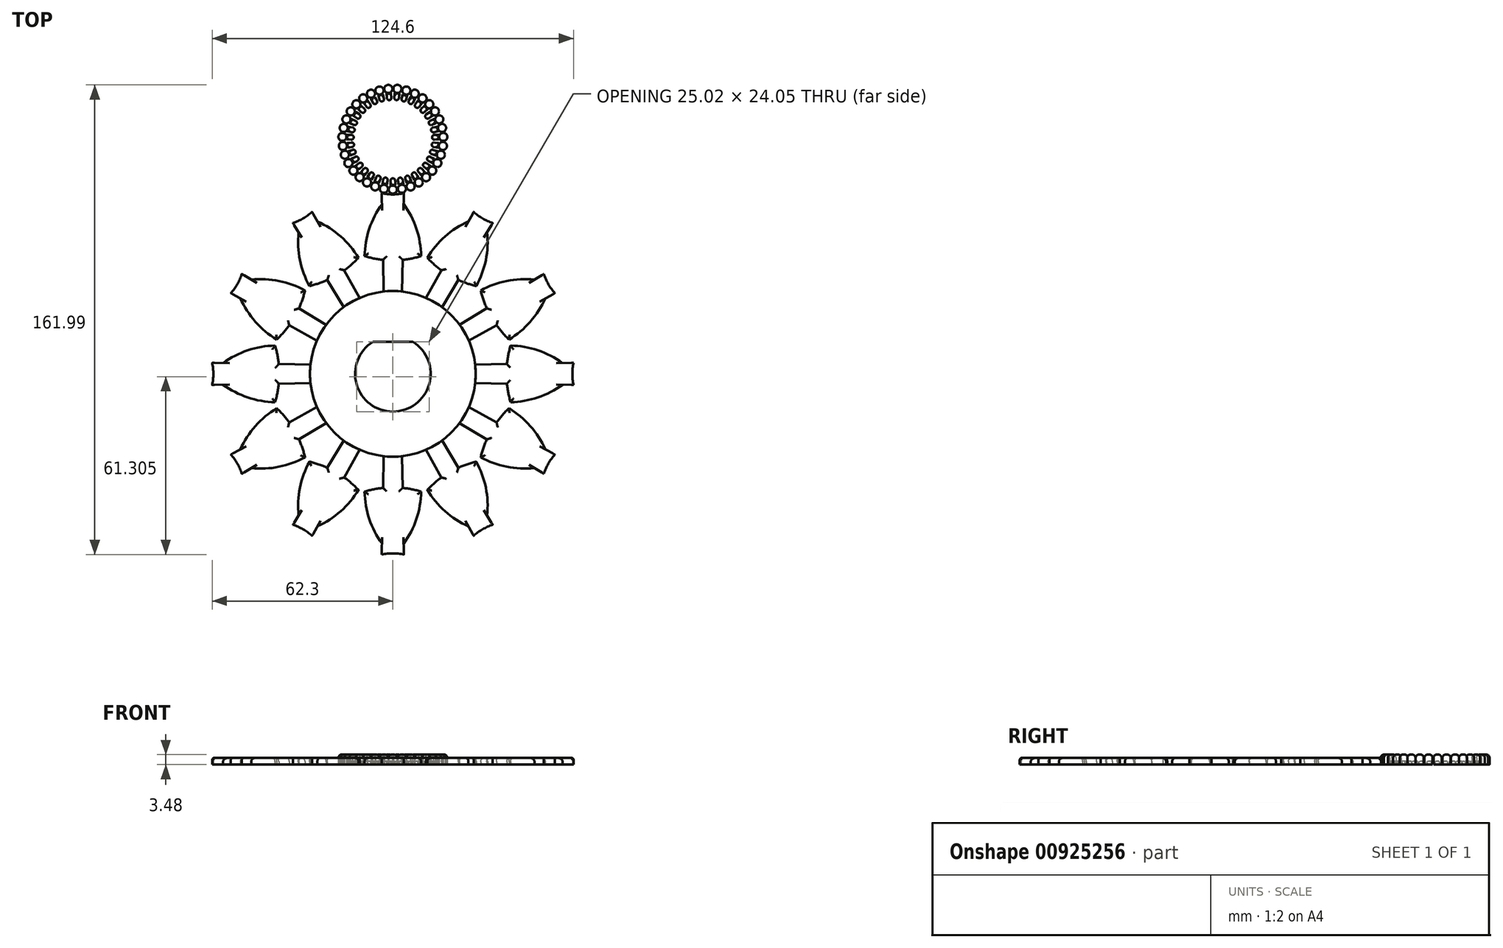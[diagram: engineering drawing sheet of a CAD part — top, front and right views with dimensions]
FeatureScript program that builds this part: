
annotation { "Feature Type Name" : "Feature", "Feature Type Description" : "" }
export const myFeature = defineFeature(function(context is Context, id is Id, definition is map)
    precondition{}
    {
        {
            var Q0;
            Q0=qCreatedBy(makeId("Top.planeOp"),FACE);
            var sketch = newSketch(context, id + "F0", { "sketchPlane" : qUnion([Q0])});
            skCircle(sketch, "E0", {"center": v(0, 0) * mm, "radius": 100.01 * mm, "construction": true});
            skCircle(sketch, "E1", {"center": v(0, 0) * mm, "radius": 80.96 * mm, "construction": true});
            skCircle(sketch, "E2", {"center": v(0, 0) * mm, "radius": 65.09 * mm, "construction": true});
            skCircle(sketch, "E3", {"center": v(0, 80.96) * mm, "radius": 19.05 * mm});
            skCircle(sketch, "E4.0", {"center": v(0, 80.96) * mm, "radius": 15.86 * mm});
            skArc(sketch, "E5", {"start": v(0.8, 66.65) * mm, "mid": v(0, 67.44) * mm, "end": v(-0.8, 66.65) * mm});
            skLineSegment(sketch, "E6", {"start": v(-0.8, 66.65) * mm, "end": v(-0.8, 65.12) * mm});
            skLineSegment(sketch, "E7", {"start": v(0.8, 66.65) * mm, "end": v(0.8, 65.12) * mm});
            skLineSegment(sketch, "E8.1.0", {"start": v(1.78, 66.73) * mm, "end": v(2.05, 65.24) * mm});
            skArc(sketch, "E8.1.1", {"start": v(3.34, 67.02) * mm, "mid": v(2.41, 67.66) * mm, "end": v(1.78, 66.73) * mm});
            skLineSegment(sketch, "E8.1.2", {"start": v(3.34, 67.02) * mm, "end": v(3.6, 65.52) * mm});
            skLineSegment(sketch, "E8.2.0", {"start": v(4.29, 67.28) * mm, "end": v(4.82, 65.85) * mm});
            skArc(sketch, "E8.2.1", {"start": v(5.77, 67.84) * mm, "mid": v(4.75, 68.3) * mm, "end": v(4.29, 67.28) * mm});
            skLineSegment(sketch, "E8.2.2", {"start": v(5.77, 67.84) * mm, "end": v(6.3, 66.41) * mm});
            skLineSegment(sketch, "E8.3.0", {"start": v(6.66, 68.27) * mm, "end": v(7.44, 66.96) * mm});
            skArc(sketch, "E8.3.1", {"start": v(8.02, 69.08) * mm, "mid": v(6.94, 69.35) * mm, "end": v(6.66, 68.27) * mm});
            skLineSegment(sketch, "E8.3.2", {"start": v(8.02, 69.08) * mm, "end": v(8.8, 67.77) * mm});
            skLineSegment(sketch, "E8.4.0", {"start": v(8.82, 69.66) * mm, "end": v(9.82, 68.51) * mm});
            skArc(sketch, "E8.4.1", {"start": v(10.02, 70.7) * mm, "mid": v(8.9, 70.78) * mm, "end": v(8.82, 69.66) * mm});
            skLineSegment(sketch, "E8.4.2", {"start": v(10.02, 70.7) * mm, "end": v(11.02, 69.56) * mm});
            skLineSegment(sketch, "E8.5.0", {"start": v(10.7, 71.42) * mm, "end": v(11.89, 70.47) * mm});
            skArc(sketch, "E8.5.1", {"start": v(11.69, 72.66) * mm, "mid": v(10.57, 72.53) * mm, "end": v(10.7, 71.42) * mm});
            skLineSegment(sketch, "E8.5.2", {"start": v(11.69, 72.66) * mm, "end": v(12.88, 71.7) * mm});
            skLineSegment(sketch, "E8.6.0", {"start": v(12.23, 73.48) * mm, "end": v(13.57, 72.76) * mm});
            skArc(sketch, "E8.6.1", {"start": v(12.98, 74.88) * mm, "mid": v(11.9, 74.55) * mm, "end": v(12.23, 73.48) * mm});
            skLineSegment(sketch, "E8.6.2", {"start": v(12.98, 74.88) * mm, "end": v(14.32, 74.16) * mm});
            skLineSegment(sketch, "E8.7.0", {"start": v(13.37, 75.78) * mm, "end": v(14.82, 75.31) * mm});
            skArc(sketch, "E8.7.1", {"start": v(13.86, 77.3) * mm, "mid": v(12.86, 76.78) * mm, "end": v(13.37, 75.78) * mm});
            skLineSegment(sketch, "E8.7.2", {"start": v(13.86, 77.3) * mm, "end": v(15.3, 76.82) * mm});
            skLineSegment(sketch, "E8.8.0", {"start": v(14.08, 78.25) * mm, "end": v(15.59, 78.05) * mm});
            skArc(sketch, "E8.8.1", {"start": v(14.3, 79.83) * mm, "mid": v(13.4, 79.15) * mm, "end": v(14.08, 78.25) * mm});
            skLineSegment(sketch, "E8.8.2", {"start": v(14.3, 79.83) * mm, "end": v(15.8, 79.62) * mm});
            skLineSegment(sketch, "E8.9.0", {"start": v(14.34, 80.81) * mm, "end": v(15.86, 80.88) * mm});
            skArc(sketch, "E8.9.1", {"start": v(14.27, 82.4) * mm, "mid": v(13.5, 81.57) * mm, "end": v(14.34, 80.81) * mm});
            skLineSegment(sketch, "E8.9.2", {"start": v(14.27, 82.4) * mm, "end": v(15.79, 82.47) * mm});
            skLineSegment(sketch, "E8.10.0", {"start": v(14.13, 83.37) * mm, "end": v(15.62, 83.71) * mm});
            skArc(sketch, "E8.10.1", {"start": v(13.78, 84.92) * mm, "mid": v(13.18, 83.97) * mm, "end": v(14.13, 83.37) * mm});
            skLineSegment(sketch, "E8.10.2", {"start": v(13.78, 84.92) * mm, "end": v(15.27, 85.26) * mm});
            skLineSegment(sketch, "E8.11.0", {"start": v(13.48, 85.86) * mm, "end": v(14.88, 86.46) * mm});
            skArc(sketch, "E8.11.1", {"start": v(12.85, 87.32) * mm, "mid": v(12.43, 86.28) * mm, "end": v(13.48, 85.86) * mm});
            skLineSegment(sketch, "E8.11.2", {"start": v(12.85, 87.32) * mm, "end": v(14.25, 87.92) * mm});
            skLineSegment(sketch, "E8.12.0", {"start": v(12.38, 88.19) * mm, "end": v(13.66, 89.03) * mm});
            skArc(sketch, "E8.12.1", {"start": v(11.51, 89.51) * mm, "mid": v(11.29, 88.41) * mm, "end": v(12.38, 88.19) * mm});
            skLineSegment(sketch, "E8.12.2", {"start": v(11.51, 89.51) * mm, "end": v(12.78, 90.35) * mm});
            skLineSegment(sketch, "E8.13.0", {"start": v(10.9, 90.28) * mm, "end": v(12, 91.34) * mm});
            skArc(sketch, "E8.13.1", {"start": v(9.8, 91.43) * mm, "mid": v(9.77, 90.3) * mm, "end": v(10.9, 90.28) * mm});
            skLineSegment(sketch, "E8.13.2", {"start": v(9.8, 91.43) * mm, "end": v(10.9, 92.48) * mm});
            skLineSegment(sketch, "E8.14.0", {"start": v(9.06, 92.08) * mm, "end": v(9.95, 93.31) * mm});
            skArc(sketch, "E8.14.1", {"start": v(7.77, 93.01) * mm, "mid": v(7.95, 91.9) * mm, "end": v(9.06, 92.08) * mm});
            skLineSegment(sketch, "E8.14.2", {"start": v(7.77, 93.01) * mm, "end": v(8.67, 94.24) * mm});
            skLineSegment(sketch, "E8.15.0", {"start": v(6.93, 93.52) * mm, "end": v(7.59, 94.89) * mm});
            skArc(sketch, "E8.15.1", {"start": v(5.5, 94.2) * mm, "mid": v(5.87, 93.15) * mm, "end": v(6.93, 93.52) * mm});
            skLineSegment(sketch, "E8.15.2", {"start": v(5.5, 94.2) * mm, "end": v(6.16, 95.58) * mm});
            skLineSegment(sketch, "E8.16.0", {"start": v(4.57, 94.55) * mm, "end": v(4.98, 96.02) * mm});
            skArc(sketch, "E8.16.1", {"start": v(3.04, 94.97) * mm, "mid": v(3.6, 94) * mm, "end": v(4.57, 94.55) * mm});
            skLineSegment(sketch, "E8.16.2", {"start": v(3.04, 94.97) * mm, "end": v(3.45, 96.44) * mm});
            skLineSegment(sketch, "E8.17.0", {"start": v(2.07, 95.15) * mm, "end": v(2.21, 96.67) * mm});
            skArc(sketch, "E8.17.1", {"start": v(0.5, 95.3) * mm, "mid": v(1.21, 94.43) * mm, "end": v(2.07, 95.15) * mm});
            skLineSegment(sketch, "E8.17.2", {"start": v(0.5, 95.3) * mm, "end": v(0.63, 96.8) * mm});
            skLineSegment(sketch, "E8.18.0", {"start": v(-0.5, 95.3) * mm, "end": v(-0.63, 96.8) * mm});
            skArc(sketch, "E8.18.1", {"start": v(-2.07, 95.15) * mm, "mid": v(-1.21, 94.43) * mm, "end": v(-0.5, 95.3) * mm});
            skLineSegment(sketch, "E8.18.2", {"start": v(-2.07, 95.15) * mm, "end": v(-2.21, 96.67) * mm});
            skLineSegment(sketch, "E8.19.0", {"start": v(-3.04, 94.97) * mm, "end": v(-3.45, 96.44) * mm});
            skArc(sketch, "E8.19.1", {"start": v(-4.57, 94.55) * mm, "mid": v(-3.6, 94) * mm, "end": v(-3.04, 94.97) * mm});
            skLineSegment(sketch, "E8.19.2", {"start": v(-4.57, 94.55) * mm, "end": v(-4.98, 96.02) * mm});
            skLineSegment(sketch, "E8.20.0", {"start": v(-5.5, 94.2) * mm, "end": v(-6.16, 95.58) * mm});
            skArc(sketch, "E8.20.1", {"start": v(-6.93, 93.52) * mm, "mid": v(-5.87, 93.15) * mm, "end": v(-5.5, 94.2) * mm});
            skLineSegment(sketch, "E8.20.2", {"start": v(-6.93, 93.52) * mm, "end": v(-7.59, 94.89) * mm});
            skLineSegment(sketch, "E8.21.0", {"start": v(-7.77, 93.01) * mm, "end": v(-8.67, 94.24) * mm});
            skArc(sketch, "E8.21.1", {"start": v(-9.06, 92.08) * mm, "mid": v(-7.95, 91.9) * mm, "end": v(-7.77, 93.01) * mm});
            skLineSegment(sketch, "E8.21.2", {"start": v(-9.06, 92.08) * mm, "end": v(-9.95, 93.31) * mm});
            skLineSegment(sketch, "E8.22.0", {"start": v(-9.8, 91.43) * mm, "end": v(-10.9, 92.48) * mm});
            skArc(sketch, "E8.22.1", {"start": v(-10.9, 90.28) * mm, "mid": v(-9.77, 90.3) * mm, "end": v(-9.8, 91.43) * mm});
            skLineSegment(sketch, "E8.22.2", {"start": v(-10.9, 90.28) * mm, "end": v(-12, 91.34) * mm});
            skLineSegment(sketch, "E8.23.0", {"start": v(-11.51, 89.51) * mm, "end": v(-12.78, 90.35) * mm});
            skArc(sketch, "E8.23.1", {"start": v(-12.38, 88.19) * mm, "mid": v(-11.29, 88.41) * mm, "end": v(-11.51, 89.51) * mm});
            skLineSegment(sketch, "E8.23.2", {"start": v(-12.38, 88.19) * mm, "end": v(-13.66, 89.03) * mm});
            skLineSegment(sketch, "E8.24.0", {"start": v(-12.85, 87.32) * mm, "end": v(-14.25, 87.92) * mm});
            skArc(sketch, "E8.24.1", {"start": v(-13.48, 85.86) * mm, "mid": v(-12.43, 86.28) * mm, "end": v(-12.85, 87.32) * mm});
            skLineSegment(sketch, "E8.24.2", {"start": v(-13.48, 85.86) * mm, "end": v(-14.88, 86.46) * mm});
            skLineSegment(sketch, "E8.25.0", {"start": v(-13.78, 84.92) * mm, "end": v(-15.27, 85.26) * mm});
            skArc(sketch, "E8.25.1", {"start": v(-14.13, 83.37) * mm, "mid": v(-13.18, 83.97) * mm, "end": v(-13.78, 84.92) * mm});
            skLineSegment(sketch, "E8.25.2", {"start": v(-14.13, 83.37) * mm, "end": v(-15.62, 83.71) * mm});
            skLineSegment(sketch, "E8.26.0", {"start": v(-14.27, 82.4) * mm, "end": v(-15.79, 82.47) * mm});
            skArc(sketch, "E8.26.1", {"start": v(-14.34, 80.81) * mm, "mid": v(-13.5, 81.57) * mm, "end": v(-14.27, 82.4) * mm});
            skLineSegment(sketch, "E8.26.2", {"start": v(-14.34, 80.81) * mm, "end": v(-15.86, 80.88) * mm});
            skLineSegment(sketch, "E8.27.0", {"start": v(-14.3, 79.83) * mm, "end": v(-15.8, 79.62) * mm});
            skArc(sketch, "E8.27.1", {"start": v(-14.08, 78.25) * mm, "mid": v(-13.4, 79.15) * mm, "end": v(-14.3, 79.83) * mm});
            skLineSegment(sketch, "E8.27.2", {"start": v(-14.08, 78.25) * mm, "end": v(-15.59, 78.05) * mm});
            skLineSegment(sketch, "E8.28.0", {"start": v(-13.86, 77.3) * mm, "end": v(-15.3, 76.82) * mm});
            skArc(sketch, "E8.28.1", {"start": v(-13.37, 75.78) * mm, "mid": v(-12.86, 76.78) * mm, "end": v(-13.86, 77.3) * mm});
            skLineSegment(sketch, "E8.28.2", {"start": v(-13.37, 75.78) * mm, "end": v(-14.82, 75.31) * mm});
            skLineSegment(sketch, "E8.29.0", {"start": v(-12.98, 74.88) * mm, "end": v(-14.32, 74.16) * mm});
            skArc(sketch, "E8.29.1", {"start": v(-12.23, 73.48) * mm, "mid": v(-11.9, 74.55) * mm, "end": v(-12.98, 74.88) * mm});
            skLineSegment(sketch, "E8.29.2", {"start": v(-12.23, 73.48) * mm, "end": v(-13.57, 72.76) * mm});
            skLineSegment(sketch, "E8.30.0", {"start": v(-11.69, 72.66) * mm, "end": v(-12.88, 71.7) * mm});
            skArc(sketch, "E8.30.1", {"start": v(-10.7, 71.42) * mm, "mid": v(-10.57, 72.53) * mm, "end": v(-11.69, 72.66) * mm});
            skLineSegment(sketch, "E8.30.2", {"start": v(-10.7, 71.42) * mm, "end": v(-11.89, 70.47) * mm});
            skLineSegment(sketch, "E8.31.0", {"start": v(-10.02, 70.7) * mm, "end": v(-11.02, 69.56) * mm});
            skArc(sketch, "E8.31.1", {"start": v(-8.82, 69.66) * mm, "mid": v(-8.9, 70.78) * mm, "end": v(-10.02, 70.7) * mm});
            skLineSegment(sketch, "E8.31.2", {"start": v(-8.82, 69.66) * mm, "end": v(-9.82, 68.51) * mm});
            skLineSegment(sketch, "E8.32.0", {"start": v(-8.02, 69.08) * mm, "end": v(-8.8, 67.77) * mm});
            skArc(sketch, "E8.32.1", {"start": v(-6.66, 68.27) * mm, "mid": v(-6.94, 69.35) * mm, "end": v(-8.02, 69.08) * mm});
            skLineSegment(sketch, "E8.32.2", {"start": v(-6.66, 68.27) * mm, "end": v(-7.44, 66.96) * mm});
            skLineSegment(sketch, "E8.33.0", {"start": v(-5.77, 67.84) * mm, "end": v(-6.3, 66.41) * mm});
            skArc(sketch, "E8.33.1", {"start": v(-4.29, 67.28) * mm, "mid": v(-4.75, 68.3) * mm, "end": v(-5.77, 67.84) * mm});
            skLineSegment(sketch, "E8.33.2", {"start": v(-4.29, 67.28) * mm, "end": v(-4.82, 65.85) * mm});
            skLineSegment(sketch, "E8.34.0", {"start": v(-3.34, 67.02) * mm, "end": v(-3.6, 65.52) * mm});
            skArc(sketch, "E8.34.1", {"start": v(-1.78, 66.73) * mm, "mid": v(-2.41, 67.66) * mm, "end": v(-3.34, 67.02) * mm});
            skLineSegment(sketch, "E8.34.2", {"start": v(-1.78, 66.73) * mm, "end": v(-2.05, 65.24) * mm});
            skCircle(sketch, "E9", {"center": v(0, 63.56) * mm, "radius": 1.4 * mm});
            skCircle(sketch, "E10.1.0", {"center": v(3.1, 63.84) * mm, "radius": 1.4 * mm});
            skCircle(sketch, "E10.2.0", {"center": v(6.11, 64.67) * mm, "radius": 1.4 * mm});
            skCircle(sketch, "E10.3.0", {"center": v(8.92, 66.03) * mm, "radius": 1.4 * mm});
            skCircle(sketch, "E10.4.0", {"center": v(11.45, 67.86) * mm, "radius": 1.4 * mm});
            skCircle(sketch, "E10.5.0", {"center": v(13.6, 70.11) * mm, "radius": 1.4 * mm});
            skCircle(sketch, "E10.6.0", {"center": v(15.32, 72.72) * mm, "radius": 1.4 * mm});
            skCircle(sketch, "E10.7.0", {"center": v(16.55, 75.59) * mm, "radius": 1.4 * mm});
            skCircle(sketch, "E10.8.0", {"center": v(17.24, 78.63) * mm, "radius": 1.4 * mm});
            skCircle(sketch, "E10.9.0", {"center": v(17.38, 81.74) * mm, "radius": 1.4 * mm});
            skCircle(sketch, "E10.10.0", {"center": v(16.96, 84.83) * mm, "radius": 1.4 * mm});
            skCircle(sketch, "E10.11.0", {"center": v(16, 87.8) * mm, "radius": 1.4 * mm});
            skCircle(sketch, "E10.12.0", {"center": v(14.52, 90.55) * mm, "radius": 1.4 * mm});
            skCircle(sketch, "E10.13.0", {"center": v(12.58, 92.99) * mm, "radius": 1.4 * mm});
            skCircle(sketch, "E10.14.0", {"center": v(10.23, 95.04) * mm, "radius": 1.4 * mm});
            skCircle(sketch, "E10.15.0", {"center": v(7.55, 96.64) * mm, "radius": 1.4 * mm});
            skCircle(sketch, "E10.16.0", {"center": v(4.63, 97.73) * mm, "radius": 1.4 * mm});
            skCircle(sketch, "E10.17.0", {"center": v(1.56, 98.3) * mm, "radius": 1.4 * mm});
            skCircle(sketch, "E10.18.0", {"center": v(-1.56, 98.3) * mm, "radius": 1.4 * mm});
            skCircle(sketch, "E10.19.0", {"center": v(-4.63, 97.73) * mm, "radius": 1.4 * mm});
            skCircle(sketch, "E10.20.0", {"center": v(-7.55, 96.64) * mm, "radius": 1.4 * mm});
            skCircle(sketch, "E10.21.0", {"center": v(-10.23, 95.04) * mm, "radius": 1.4 * mm});
            skCircle(sketch, "E10.22.0", {"center": v(-12.58, 92.99) * mm, "radius": 1.4 * mm});
            skCircle(sketch, "E10.23.0", {"center": v(-14.52, 90.55) * mm, "radius": 1.4 * mm});
            skCircle(sketch, "E10.24.0", {"center": v(-16, 87.8) * mm, "radius": 1.4 * mm});
            skCircle(sketch, "E10.25.0", {"center": v(-16.96, 84.83) * mm, "radius": 1.4 * mm});
            skCircle(sketch, "E10.26.0", {"center": v(-17.38, 81.74) * mm, "radius": 1.4 * mm});
            skCircle(sketch, "E10.27.0", {"center": v(-17.24, 78.63) * mm, "radius": 1.4 * mm});
            skCircle(sketch, "E10.28.0", {"center": v(-16.55, 75.59) * mm, "radius": 1.4 * mm});
            skCircle(sketch, "E10.29.0", {"center": v(-15.32, 72.72) * mm, "radius": 1.4 * mm});
            skCircle(sketch, "E10.30.0", {"center": v(-13.6, 70.11) * mm, "radius": 1.4 * mm});
            skCircle(sketch, "E10.31.0", {"center": v(-11.45, 67.86) * mm, "radius": 1.4 * mm});
            skCircle(sketch, "E10.32.0", {"center": v(-8.92, 66.03) * mm, "radius": 1.4 * mm});
            skCircle(sketch, "E10.33.0", {"center": v(-6.11, 64.67) * mm, "radius": 1.4 * mm});
            skCircle(sketch, "E10.34.0", {"center": v(-3.1, 63.84) * mm, "radius": 1.4 * mm});
            skLineSegment(sketch, "E11.0", {"start": v(3.18, 28.4) * mm, "end": v(3.81, 62.3) * mm});
            skLineSegment(sketch, "E12.0", {"start": v(-3.18, 28.4) * mm, "end": v(-3.81, 62.3) * mm});
            skCircle(sketch, "E13", {"center": v(0, 0) * mm, "radius": 28.58 * mm});
            skLineSegment(sketch, "E14.0", {"start": v(9.44, 23.59) * mm, "end": v(10.16, 62.18) * mm, "construction": true});
            skLineSegment(sketch, "E15.0", {"start": v(-9.44, 23.59) * mm, "end": v(-10.16, 62.18) * mm, "construction": true});
            skLineSegment(sketch, "E16", {"start": v(-12.43, 40.62) * mm, "end": v(16.46, 40.62) * mm, "construction": true});
            skLineSegment(sketch, "E17", {"start": v(-3.74, 58.53) * mm, "end": v(3.74, 58.53) * mm, "construction": true});
            skArc(sketch, "E18", {"start": v(-3.74, 58.53) * mm, "mid": v(-8.13, 50.03) * mm, "end": v(-9.75, 40.62) * mm});
            skArc(sketch, "E19", {"start": v(9.75, 40.62) * mm, "mid": v(8.12, 50.03) * mm, "end": v(3.74, 58.53) * mm});
            skArc(sketch, "E20", {"start": v(-9.75, 40.62) * mm, "mid": v(0, 39.17) * mm, "end": v(9.75, 40.62) * mm});
            skSolve(sketch);
        }
        {
            var Q0;
            {var subQ0=sQuery(id+"F0.wireOp",EDGE,"E13");var subQ1=sQuery(id+"F0.wireOp",EDGE,"E11.0");var subQ2=makeQuery(id+"F0.imprint","INTERSECT",VERTEX,{"derivedFrom":[subQ1,subQ0]});Q0=makeQuery(id+"F0.imprint","IMPRINT",FACE,{"disambiguationData":[TD([[makeQuery(id+"F0.imprint","IMPRINT",EDGE,{"disambiguationData":[TD([[subQ2,-1.0]])],"derivedFrom":subQ1}),1.0]])]});}
            var Q1;
            {var subQ4=sQuery(id+"F0.wireOp",EDGE,"E11.0");var subQ5=sQuery(id+"F0.wireOp",EDGE,"E3");var subQ6=makeQuery(id+"F0.imprint","INTERSECT",VERTEX,{"derivedFrom":[subQ5,subQ4]});Q1=makeQuery(id+"F0.imprint","IMPRINT",FACE,{"disambiguationData":[TD([[makeQuery(id+"F0.imprint","IMPRINT",EDGE,{"disambiguationData":[TD([[subQ6,1.0]])],"derivedFrom":subQ5}),-1.0]])]});}
            var Q2;
            {var subQ0=sQuery(id+"F0.wireOp",EDGE,"E19");Q2=makeQuery(id+"F0.imprint","IMPRINT",FACE,{"disambiguationData":[TD([[makeQuery(id+"F0.imprint","IMPRINT",EDGE,{"derivedFrom":subQ0}),1.0]])]});}
            var Q3;
            {var subQ0=sQuery(id+"F0.wireOp",EDGE,"E18");Q3=makeQuery(id+"F0.imprint","IMPRINT",FACE,{"disambiguationData":[TD([[makeQuery(id+"F0.imprint","IMPRINT",EDGE,{"derivedFrom":subQ0}),1.0]])]});}
            var Q4;
            Q4=makeQuery(id+"F0.imprint","IMPRINT",FACE,{"disambiguationData":[TD([[makeQuery(id+"F0.imprint","IMPRINT",EDGE,{"derivedFrom":sQuery(id+"F0.wireOp",EDGE,"E9")}),-1.0]])]});
            extrude(context, id + "F1", {"entities" : qUnion([Q0, Q1, Q2, Q3, Q4]), "depth" : 2.38 * mm, "offsetDistance" : 25.4 * mm});
        }
        {
            var Q0;
            Q0=makeQuery(id+"F0.imprint","IMPRINT",FACE,{"disambiguationData":[TD([[makeQuery(id+"F0.imprint","IMPRINT",EDGE,{"derivedFrom":sQuery(id+"F0.wireOp",EDGE,"E10.22.0")}),1.0]])]});
            var Q1;
            Q1=makeQuery(id+"F0.imprint","IMPRINT",FACE,{"disambiguationData":[TD([[makeQuery(id+"F0.imprint","IMPRINT",EDGE,{"derivedFrom":sQuery(id+"F0.wireOp",EDGE,"E10.21.0")}),1.0]])]});
            var Q2;
            Q2=makeQuery(id+"F0.imprint","IMPRINT",FACE,{"disambiguationData":[TD([[makeQuery(id+"F0.imprint","IMPRINT",EDGE,{"derivedFrom":sQuery(id+"F0.wireOp",EDGE,"E10.19.0")}),1.0]])]});
            var Q3;
            Q3=makeQuery(id+"F0.imprint","IMPRINT",FACE,{"disambiguationData":[TD([[makeQuery(id+"F0.imprint","IMPRINT",EDGE,{"derivedFrom":sQuery(id+"F0.wireOp",EDGE,"E10.18.0")}),1.0]])]});
            var Q4;
            Q4=makeQuery(id+"F0.imprint","IMPRINT",FACE,{"disambiguationData":[TD([[makeQuery(id+"F0.imprint","IMPRINT",EDGE,{"derivedFrom":sQuery(id+"F0.wireOp",EDGE,"E10.20.0")}),1.0]])]});
            var Q5;
            Q5=makeQuery(id+"F0.imprint","IMPRINT",FACE,{"disambiguationData":[TD([[makeQuery(id+"F0.imprint","IMPRINT",EDGE,{"derivedFrom":sQuery(id+"F0.wireOp",EDGE,"E10.17.0")}),1.0]])]});
            var Q6;
            Q6=makeQuery(id+"F0.imprint","IMPRINT",FACE,{"disambiguationData":[TD([[makeQuery(id+"F0.imprint","IMPRINT",EDGE,{"derivedFrom":sQuery(id+"F0.wireOp",EDGE,"E10.16.0")}),1.0]])]});
            var Q7;
            Q7=makeQuery(id+"F0.imprint","IMPRINT",FACE,{"disambiguationData":[TD([[makeQuery(id+"F0.imprint","IMPRINT",EDGE,{"derivedFrom":sQuery(id+"F0.wireOp",EDGE,"E10.15.0")}),1.0]])]});
            var Q8;
            Q8=makeQuery(id+"F0.imprint","IMPRINT",FACE,{"disambiguationData":[TD([[makeQuery(id+"F0.imprint","IMPRINT",EDGE,{"derivedFrom":sQuery(id+"F0.wireOp",EDGE,"E10.14.0")}),1.0]])]});
            var Q9;
            Q9=makeQuery(id+"F0.imprint","IMPRINT",FACE,{"disambiguationData":[TD([[makeQuery(id+"F0.imprint","IMPRINT",EDGE,{"derivedFrom":sQuery(id+"F0.wireOp",EDGE,"E10.13.0")}),1.0]])]});
            var Q10;
            Q10=makeQuery(id+"F0.imprint","IMPRINT",FACE,{"disambiguationData":[TD([[makeQuery(id+"F0.imprint","IMPRINT",EDGE,{"derivedFrom":sQuery(id+"F0.wireOp",EDGE,"E10.12.0")}),1.0]])]});
            var Q11;
            Q11=makeQuery(id+"F0.imprint","IMPRINT",FACE,{"disambiguationData":[TD([[makeQuery(id+"F0.imprint","IMPRINT",EDGE,{"derivedFrom":sQuery(id+"F0.wireOp",EDGE,"E10.11.0")}),1.0]])]});
            var Q12;
            Q12=makeQuery(id+"F0.imprint","IMPRINT",FACE,{"disambiguationData":[TD([[makeQuery(id+"F0.imprint","IMPRINT",EDGE,{"derivedFrom":sQuery(id+"F0.wireOp",EDGE,"E10.10.0")}),1.0]])]});
            var Q13;
            Q13=makeQuery(id+"F0.imprint","IMPRINT",FACE,{"disambiguationData":[TD([[makeQuery(id+"F0.imprint","IMPRINT",EDGE,{"derivedFrom":sQuery(id+"F0.wireOp",EDGE,"E10.9.0")}),1.0]])]});
            var Q14;
            Q14=makeQuery(id+"F0.imprint","IMPRINT",FACE,{"disambiguationData":[TD([[makeQuery(id+"F0.imprint","IMPRINT",EDGE,{"derivedFrom":sQuery(id+"F0.wireOp",EDGE,"E10.8.0")}),1.0]])]});
            var Q15;
            Q15=makeQuery(id+"F0.imprint","IMPRINT",FACE,{"disambiguationData":[TD([[makeQuery(id+"F0.imprint","IMPRINT",EDGE,{"derivedFrom":sQuery(id+"F0.wireOp",EDGE,"E10.23.0")}),1.0]])]});
            var Q16;
            Q16=makeQuery(id+"F0.imprint","IMPRINT",FACE,{"disambiguationData":[TD([[makeQuery(id+"F0.imprint","IMPRINT",EDGE,{"derivedFrom":sQuery(id+"F0.wireOp",EDGE,"E10.24.0")}),1.0]])]});
            var Q17;
            Q17=makeQuery(id+"F0.imprint","IMPRINT",FACE,{"disambiguationData":[TD([[makeQuery(id+"F0.imprint","IMPRINT",EDGE,{"derivedFrom":sQuery(id+"F0.wireOp",EDGE,"E10.25.0")}),1.0]])]});
            var Q18;
            Q18=makeQuery(id+"F0.imprint","IMPRINT",FACE,{"disambiguationData":[TD([[makeQuery(id+"F0.imprint","IMPRINT",EDGE,{"derivedFrom":sQuery(id+"F0.wireOp",EDGE,"E10.26.0")}),1.0]])]});
            var Q19;
            Q19=makeQuery(id+"F0.imprint","IMPRINT",FACE,{"disambiguationData":[TD([[makeQuery(id+"F0.imprint","IMPRINT",EDGE,{"derivedFrom":sQuery(id+"F0.wireOp",EDGE,"E10.27.0")}),1.0]])]});
            var Q20;
            Q20=makeQuery(id+"F0.imprint","IMPRINT",FACE,{"disambiguationData":[TD([[makeQuery(id+"F0.imprint","IMPRINT",EDGE,{"derivedFrom":sQuery(id+"F0.wireOp",EDGE,"E10.28.0")}),1.0]])]});
            var Q21;
            Q21=makeQuery(id+"F0.imprint","IMPRINT",FACE,{"disambiguationData":[TD([[makeQuery(id+"F0.imprint","IMPRINT",EDGE,{"derivedFrom":sQuery(id+"F0.wireOp",EDGE,"E10.29.0")}),1.0]])]});
            var Q22;
            Q22=makeQuery(id+"F0.imprint","IMPRINT",FACE,{"disambiguationData":[TD([[makeQuery(id+"F0.imprint","IMPRINT",EDGE,{"derivedFrom":sQuery(id+"F0.wireOp",EDGE,"E10.30.0")}),1.0]])]});
            var Q23;
            Q23=makeQuery(id+"F0.imprint","IMPRINT",FACE,{"disambiguationData":[TD([[makeQuery(id+"F0.imprint","IMPRINT",EDGE,{"derivedFrom":sQuery(id+"F0.wireOp",EDGE,"E10.31.0")}),1.0]])]});
            var Q24;
            Q24=makeQuery(id+"F0.imprint","IMPRINT",FACE,{"disambiguationData":[TD([[makeQuery(id+"F0.imprint","IMPRINT",EDGE,{"derivedFrom":sQuery(id+"F0.wireOp",EDGE,"E10.33.0")}),1.0]])]});
            var Q25;
            Q25=makeQuery(id+"F0.imprint","IMPRINT",FACE,{"disambiguationData":[TD([[makeQuery(id+"F0.imprint","IMPRINT",EDGE,{"derivedFrom":sQuery(id+"F0.wireOp",EDGE,"E10.34.0")}),1.0]])]});
            var Q26;
            Q26=makeQuery(id+"F0.imprint","IMPRINT",FACE,{"disambiguationData":[TD([[makeQuery(id+"F0.imprint","IMPRINT",EDGE,{"derivedFrom":sQuery(id+"F0.wireOp",EDGE,"E9")}),1.0]])]});
            var Q27;
            Q27=makeQuery(id+"F0.imprint","IMPRINT",FACE,{"disambiguationData":[TD([[makeQuery(id+"F0.imprint","IMPRINT",EDGE,{"derivedFrom":sQuery(id+"F0.wireOp",EDGE,"E10.32.0")}),1.0]])]});
            var Q28;
            Q28=makeQuery(id+"F0.imprint","IMPRINT",FACE,{"disambiguationData":[TD([[makeQuery(id+"F0.imprint","IMPRINT",EDGE,{"derivedFrom":sQuery(id+"F0.wireOp",EDGE,"E10.1.0")}),1.0]])]});
            var Q29;
            Q29=makeQuery(id+"F0.imprint","IMPRINT",FACE,{"disambiguationData":[TD([[makeQuery(id+"F0.imprint","IMPRINT",EDGE,{"derivedFrom":sQuery(id+"F0.wireOp",EDGE,"E10.2.0")}),1.0]])]});
            var Q30;
            Q30=makeQuery(id+"F0.imprint","IMPRINT",FACE,{"disambiguationData":[TD([[makeQuery(id+"F0.imprint","IMPRINT",EDGE,{"derivedFrom":sQuery(id+"F0.wireOp",EDGE,"E10.3.0")}),1.0]])]});
            var Q31;
            Q31=makeQuery(id+"F0.imprint","IMPRINT",FACE,{"disambiguationData":[TD([[makeQuery(id+"F0.imprint","IMPRINT",EDGE,{"derivedFrom":sQuery(id+"F0.wireOp",EDGE,"E10.4.0")}),1.0]])]});
            var Q32;
            Q32=makeQuery(id+"F0.imprint","IMPRINT",FACE,{"disambiguationData":[TD([[makeQuery(id+"F0.imprint","IMPRINT",EDGE,{"derivedFrom":sQuery(id+"F0.wireOp",EDGE,"E10.5.0")}),1.0]])]});
            var Q33;
            Q33=makeQuery(id+"F0.imprint","IMPRINT",FACE,{"disambiguationData":[TD([[makeQuery(id+"F0.imprint","IMPRINT",EDGE,{"derivedFrom":sQuery(id+"F0.wireOp",EDGE,"E10.6.0")}),1.0]])]});
            var Q34;
            Q34=makeQuery(id+"F0.imprint","IMPRINT",FACE,{"disambiguationData":[TD([[makeQuery(id+"F0.imprint","IMPRINT",EDGE,{"derivedFrom":sQuery(id+"F0.wireOp",EDGE,"E10.7.0")}),1.0]])]});
            extrude(context, id + "F2", {"entities" : qUnion([Q0, Q1, Q2, Q3, Q4, Q5, Q6, Q7, Q8, Q9, Q10, Q11, Q12, Q13, Q14, Q15, Q16, Q17, Q18, Q19, Q20, Q21, Q22, Q23, Q24, Q25, Q26, Q27, Q28, Q29, Q30, Q31, Q32, Q33, Q34]), "operationType" : NewBodyOperationType.ADD, "depth" : 3.48 * mm, "offsetDistance" : 25.4 * mm});
        }
        {
            var Q0;
            {var subQ0=sQuery(id+"F0.wireOp",EDGE,"E8.25.0");Q0=makeQuery(id+"F0.imprint","IMPRINT",FACE,{"disambiguationData":[TD([[makeQuery(id+"F0.imprint","IMPRINT",EDGE,{"derivedFrom":subQ0}),1.0]])]});}
            var Q1;
            {var subQ0=sQuery(id+"F0.wireOp",EDGE,"E8.24.0");Q1=makeQuery(id+"F0.imprint","IMPRINT",FACE,{"disambiguationData":[TD([[makeQuery(id+"F0.imprint","IMPRINT",EDGE,{"derivedFrom":subQ0}),1.0]])]});}
            var Q2;
            {var subQ0=sQuery(id+"F0.wireOp",EDGE,"E8.26.0");Q2=makeQuery(id+"F0.imprint","IMPRINT",FACE,{"disambiguationData":[TD([[makeQuery(id+"F0.imprint","IMPRINT",EDGE,{"derivedFrom":subQ0}),1.0]])]});}
            var Q3;
            {var subQ0=sQuery(id+"F0.wireOp",EDGE,"E8.27.0");Q3=makeQuery(id+"F0.imprint","IMPRINT",FACE,{"disambiguationData":[TD([[makeQuery(id+"F0.imprint","IMPRINT",EDGE,{"derivedFrom":subQ0}),1.0]])]});}
            var Q4;
            {var subQ0=sQuery(id+"F0.wireOp",EDGE,"E8.28.0");Q4=makeQuery(id+"F0.imprint","IMPRINT",FACE,{"disambiguationData":[TD([[makeQuery(id+"F0.imprint","IMPRINT",EDGE,{"derivedFrom":subQ0}),1.0]])]});}
            var Q5;
            {var subQ0=sQuery(id+"F0.wireOp",EDGE,"E8.29.0");Q5=makeQuery(id+"F0.imprint","IMPRINT",FACE,{"disambiguationData":[TD([[makeQuery(id+"F0.imprint","IMPRINT",EDGE,{"derivedFrom":subQ0}),1.0]])]});}
            var Q6;
            {var subQ0=sQuery(id+"F0.wireOp",EDGE,"E8.30.0");Q6=makeQuery(id+"F0.imprint","IMPRINT",FACE,{"disambiguationData":[TD([[makeQuery(id+"F0.imprint","IMPRINT",EDGE,{"derivedFrom":subQ0}),1.0]])]});}
            var Q7;
            {var subQ0=sQuery(id+"F0.wireOp",EDGE,"E8.31.0");Q7=makeQuery(id+"F0.imprint","IMPRINT",FACE,{"disambiguationData":[TD([[makeQuery(id+"F0.imprint","IMPRINT",EDGE,{"derivedFrom":subQ0}),1.0]])]});}
            var Q8;
            {var subQ0=sQuery(id+"F0.wireOp",EDGE,"E8.32.0");Q8=makeQuery(id+"F0.imprint","IMPRINT",FACE,{"disambiguationData":[TD([[makeQuery(id+"F0.imprint","IMPRINT",EDGE,{"derivedFrom":subQ0}),1.0]])]});}
            var Q9;
            {var subQ0=sQuery(id+"F0.wireOp",EDGE,"E8.33.0");Q9=makeQuery(id+"F0.imprint","IMPRINT",FACE,{"disambiguationData":[TD([[makeQuery(id+"F0.imprint","IMPRINT",EDGE,{"derivedFrom":subQ0}),1.0]])]});}
            var Q10;
            {var subQ0=sQuery(id+"F0.wireOp",EDGE,"E8.34.0");Q10=makeQuery(id+"F0.imprint","IMPRINT",FACE,{"disambiguationData":[TD([[makeQuery(id+"F0.imprint","IMPRINT",EDGE,{"derivedFrom":subQ0}),1.0]])]});}
            var Q11;
            Q11=makeQuery(id+"F0.imprint","IMPRINT",FACE,{"disambiguationData":[TD([[makeQuery(id+"F0.imprint","IMPRINT",EDGE,{"derivedFrom":sQuery(id+"F0.wireOp",EDGE,"E5")}),1.0]])]});
            var Q12;
            {var subQ0=sQuery(id+"F0.wireOp",EDGE,"E8.1.0");Q12=makeQuery(id+"F0.imprint","IMPRINT",FACE,{"disambiguationData":[TD([[makeQuery(id+"F0.imprint","IMPRINT",EDGE,{"derivedFrom":subQ0}),1.0]])]});}
            var Q13;
            {var subQ0=sQuery(id+"F0.wireOp",EDGE,"E8.2.0");Q13=makeQuery(id+"F0.imprint","IMPRINT",FACE,{"disambiguationData":[TD([[makeQuery(id+"F0.imprint","IMPRINT",EDGE,{"derivedFrom":subQ0}),1.0]])]});}
            var Q14;
            {var subQ0=sQuery(id+"F0.wireOp",EDGE,"E8.3.0");Q14=makeQuery(id+"F0.imprint","IMPRINT",FACE,{"disambiguationData":[TD([[makeQuery(id+"F0.imprint","IMPRINT",EDGE,{"derivedFrom":subQ0}),1.0]])]});}
            var Q15;
            {var subQ0=sQuery(id+"F0.wireOp",EDGE,"E8.4.0");Q15=makeQuery(id+"F0.imprint","IMPRINT",FACE,{"disambiguationData":[TD([[makeQuery(id+"F0.imprint","IMPRINT",EDGE,{"derivedFrom":subQ0}),1.0]])]});}
            var Q16;
            {var subQ0=sQuery(id+"F0.wireOp",EDGE,"E8.5.0");Q16=makeQuery(id+"F0.imprint","IMPRINT",FACE,{"disambiguationData":[TD([[makeQuery(id+"F0.imprint","IMPRINT",EDGE,{"derivedFrom":subQ0}),1.0]])]});}
            var Q17;
            {var subQ0=sQuery(id+"F0.wireOp",EDGE,"E8.6.0");Q17=makeQuery(id+"F0.imprint","IMPRINT",FACE,{"disambiguationData":[TD([[makeQuery(id+"F0.imprint","IMPRINT",EDGE,{"derivedFrom":subQ0}),1.0]])]});}
            var Q18;
            {var subQ0=sQuery(id+"F0.wireOp",EDGE,"E8.7.0");Q18=makeQuery(id+"F0.imprint","IMPRINT",FACE,{"disambiguationData":[TD([[makeQuery(id+"F0.imprint","IMPRINT",EDGE,{"derivedFrom":subQ0}),1.0]])]});}
            var Q19;
            {var subQ0=sQuery(id+"F0.wireOp",EDGE,"E8.8.0");Q19=makeQuery(id+"F0.imprint","IMPRINT",FACE,{"disambiguationData":[TD([[makeQuery(id+"F0.imprint","IMPRINT",EDGE,{"derivedFrom":subQ0}),1.0]])]});}
            var Q20;
            {var subQ0=sQuery(id+"F0.wireOp",EDGE,"E8.9.0");Q20=makeQuery(id+"F0.imprint","IMPRINT",FACE,{"disambiguationData":[TD([[makeQuery(id+"F0.imprint","IMPRINT",EDGE,{"derivedFrom":subQ0}),1.0]])]});}
            var Q21;
            {var subQ0=sQuery(id+"F0.wireOp",EDGE,"E8.10.0");Q21=makeQuery(id+"F0.imprint","IMPRINT",FACE,{"disambiguationData":[TD([[makeQuery(id+"F0.imprint","IMPRINT",EDGE,{"derivedFrom":subQ0}),1.0]])]});}
            var Q22;
            {var subQ0=sQuery(id+"F0.wireOp",EDGE,"E8.11.0");Q22=makeQuery(id+"F0.imprint","IMPRINT",FACE,{"disambiguationData":[TD([[makeQuery(id+"F0.imprint","IMPRINT",EDGE,{"derivedFrom":subQ0}),1.0]])]});}
            var Q23;
            {var subQ0=sQuery(id+"F0.wireOp",EDGE,"E8.12.0");Q23=makeQuery(id+"F0.imprint","IMPRINT",FACE,{"disambiguationData":[TD([[makeQuery(id+"F0.imprint","IMPRINT",EDGE,{"derivedFrom":subQ0}),1.0]])]});}
            var Q24;
            {var subQ0=sQuery(id+"F0.wireOp",EDGE,"E8.13.0");Q24=makeQuery(id+"F0.imprint","IMPRINT",FACE,{"disambiguationData":[TD([[makeQuery(id+"F0.imprint","IMPRINT",EDGE,{"derivedFrom":subQ0}),1.0]])]});}
            var Q25;
            {var subQ0=sQuery(id+"F0.wireOp",EDGE,"E8.14.0");Q25=makeQuery(id+"F0.imprint","IMPRINT",FACE,{"disambiguationData":[TD([[makeQuery(id+"F0.imprint","IMPRINT",EDGE,{"derivedFrom":subQ0}),1.0]])]});}
            var Q26;
            {var subQ0=sQuery(id+"F0.wireOp",EDGE,"E8.15.0");Q26=makeQuery(id+"F0.imprint","IMPRINT",FACE,{"disambiguationData":[TD([[makeQuery(id+"F0.imprint","IMPRINT",EDGE,{"derivedFrom":subQ0}),1.0]])]});}
            var Q27;
            {var subQ0=sQuery(id+"F0.wireOp",EDGE,"E8.16.0");Q27=makeQuery(id+"F0.imprint","IMPRINT",FACE,{"disambiguationData":[TD([[makeQuery(id+"F0.imprint","IMPRINT",EDGE,{"derivedFrom":subQ0}),1.0]])]});}
            var Q28;
            {var subQ0=sQuery(id+"F0.wireOp",EDGE,"E8.17.0");Q28=makeQuery(id+"F0.imprint","IMPRINT",FACE,{"disambiguationData":[TD([[makeQuery(id+"F0.imprint","IMPRINT",EDGE,{"derivedFrom":subQ0}),1.0]])]});}
            var Q29;
            {var subQ0=sQuery(id+"F0.wireOp",EDGE,"E8.18.0");Q29=makeQuery(id+"F0.imprint","IMPRINT",FACE,{"disambiguationData":[TD([[makeQuery(id+"F0.imprint","IMPRINT",EDGE,{"derivedFrom":subQ0}),1.0]])]});}
            var Q30;
            {var subQ0=sQuery(id+"F0.wireOp",EDGE,"E8.19.0");Q30=makeQuery(id+"F0.imprint","IMPRINT",FACE,{"disambiguationData":[TD([[makeQuery(id+"F0.imprint","IMPRINT",EDGE,{"derivedFrom":subQ0}),1.0]])]});}
            var Q31;
            {var subQ0=sQuery(id+"F0.wireOp",EDGE,"E8.20.0");Q31=makeQuery(id+"F0.imprint","IMPRINT",FACE,{"disambiguationData":[TD([[makeQuery(id+"F0.imprint","IMPRINT",EDGE,{"derivedFrom":subQ0}),1.0]])]});}
            var Q32;
            {var subQ0=sQuery(id+"F0.wireOp",EDGE,"E8.21.0");Q32=makeQuery(id+"F0.imprint","IMPRINT",FACE,{"disambiguationData":[TD([[makeQuery(id+"F0.imprint","IMPRINT",EDGE,{"derivedFrom":subQ0}),1.0]])]});}
            var Q33;
            {var subQ0=sQuery(id+"F0.wireOp",EDGE,"E8.22.0");Q33=makeQuery(id+"F0.imprint","IMPRINT",FACE,{"disambiguationData":[TD([[makeQuery(id+"F0.imprint","IMPRINT",EDGE,{"derivedFrom":subQ0}),1.0]])]});}
            var Q34;
            {var subQ0=sQuery(id+"F0.wireOp",EDGE,"E8.23.0");Q34=makeQuery(id+"F0.imprint","IMPRINT",FACE,{"disambiguationData":[TD([[makeQuery(id+"F0.imprint","IMPRINT",EDGE,{"derivedFrom":subQ0}),1.0]])]});}
            extrude(context, id + "F3", {"entities" : qUnion([Q0, Q1, Q2, Q3, Q4, Q5, Q6, Q7, Q8, Q9, Q10, Q11, Q12, Q13, Q14, Q15, Q16, Q17, Q18, Q19, Q20, Q21, Q22, Q23, Q24, Q25, Q26, Q27, Q28, Q29, Q30, Q31, Q32, Q33, Q34]), "operationType" : NewBodyOperationType.ADD, "depth" : 1.2 * mm, "offsetDistance" : 25.4 * mm});
        }
        {
            var Q0;
            Q0=makeQuery(id+"F2.opExtrude","CAP_FACE",FACE,{"disambiguationData":[OSD([sQuery(id+"F0.wireOp",EDGE,"E10.8.0")])],"isStart":false});
            var Q1;
            Q1=makeQuery(id+"F2.opExtrude","CAP_FACE",FACE,{"disambiguationData":[OSD([sQuery(id+"F0.wireOp",EDGE,"E10.7.0")])],"isStart":false});
            var Q2;
            Q2=makeQuery(id+"F2.opExtrude","CAP_FACE",FACE,{"disambiguationData":[OSD([sQuery(id+"F0.wireOp",EDGE,"E10.9.0")])],"isStart":false});
            var Q3;
            Q3=makeQuery(id+"F2.opExtrude","CAP_FACE",FACE,{"disambiguationData":[OSD([sQuery(id+"F0.wireOp",EDGE,"E10.10.0")])],"isStart":false});
            var Q4;
            Q4=makeQuery(id+"F2.opExtrude","CAP_FACE",FACE,{"disambiguationData":[OSD([sQuery(id+"F0.wireOp",EDGE,"E10.11.0")])],"isStart":false});
            var Q5;
            Q5=makeQuery(id+"F2.opExtrude","CAP_FACE",FACE,{"disambiguationData":[OSD([sQuery(id+"F0.wireOp",EDGE,"E10.12.0")])],"isStart":false});
            var Q6;
            Q6=makeQuery(id+"F2.opExtrude","CAP_EDGE",EDGE,{"disambiguationData":[OSD([sQuery(id+"F0.wireOp",EDGE,"E10.13.0")])],"isStart":false});
            var Q7;
            Q7=makeQuery(id+"F2.opExtrude","CAP_FACE",FACE,{"disambiguationData":[OSD([sQuery(id+"F0.wireOp",EDGE,"E10.14.0")])],"isStart":false});
            var Q8;
            Q8=makeQuery(id+"F2.opExtrude","CAP_FACE",FACE,{"disambiguationData":[OSD([sQuery(id+"F0.wireOp",EDGE,"E10.15.0")])],"isStart":false});
            var Q9;
            Q9=makeQuery(id+"F2.opExtrude","CAP_FACE",FACE,{"disambiguationData":[OSD([sQuery(id+"F0.wireOp",EDGE,"E10.16.0")])],"isStart":false});
            var Q10;
            Q10=makeQuery(id+"F2.opExtrude","CAP_FACE",FACE,{"disambiguationData":[OSD([sQuery(id+"F0.wireOp",EDGE,"E10.17.0")])],"isStart":false});
            var Q11;
            Q11=makeQuery(id+"F2.opExtrude","CAP_FACE",FACE,{"disambiguationData":[OSD([sQuery(id+"F0.wireOp",EDGE,"E10.18.0")])],"isStart":false});
            var Q12;
            Q12=makeQuery(id+"F2.opExtrude","CAP_FACE",FACE,{"disambiguationData":[OSD([sQuery(id+"F0.wireOp",EDGE,"E10.19.0")])],"isStart":false});
            var Q13;
            Q13=makeQuery(id+"F2.opExtrude","CAP_FACE",FACE,{"disambiguationData":[OSD([sQuery(id+"F0.wireOp",EDGE,"E10.20.0")])],"isStart":false});
            var Q14;
            Q14=makeQuery(id+"F2.opExtrude","CAP_FACE",FACE,{"disambiguationData":[OSD([sQuery(id+"F0.wireOp",EDGE,"E10.21.0")])],"isStart":false});
            var Q15;
            Q15=makeQuery(id+"F2.opExtrude","CAP_FACE",FACE,{"disambiguationData":[OSD([sQuery(id+"F0.wireOp",EDGE,"E10.22.0")])],"isStart":false});
            var Q16;
            Q16=makeQuery(id+"F2.opExtrude","CAP_FACE",FACE,{"disambiguationData":[OSD([sQuery(id+"F0.wireOp",EDGE,"E10.23.0")])],"isStart":false});
            var Q17;
            Q17=makeQuery(id+"F2.opExtrude","CAP_FACE",FACE,{"disambiguationData":[OSD([sQuery(id+"F0.wireOp",EDGE,"E10.24.0")])],"isStart":false});
            var Q18;
            Q18=makeQuery(id+"F2.opExtrude","CAP_FACE",FACE,{"disambiguationData":[OSD([sQuery(id+"F0.wireOp",EDGE,"E10.25.0")])],"isStart":false});
            var Q19;
            Q19=makeQuery(id+"F2.opExtrude","CAP_FACE",FACE,{"disambiguationData":[OSD([sQuery(id+"F0.wireOp",EDGE,"E10.26.0")])],"isStart":false});
            var Q20;
            Q20=makeQuery(id+"F2.opExtrude","CAP_FACE",FACE,{"disambiguationData":[OSD([sQuery(id+"F0.wireOp",EDGE,"E10.27.0")])],"isStart":false});
            var Q21;
            Q21=makeQuery(id+"F2.opExtrude","CAP_FACE",FACE,{"disambiguationData":[OSD([sQuery(id+"F0.wireOp",EDGE,"E10.28.0")])],"isStart":false});
            var Q22;
            Q22=makeQuery(id+"F2.opExtrude","CAP_FACE",FACE,{"disambiguationData":[OSD([sQuery(id+"F0.wireOp",EDGE,"E10.29.0")])],"isStart":false});
            var Q23;
            Q23=makeQuery(id+"F2.opExtrude","CAP_FACE",FACE,{"disambiguationData":[OSD([sQuery(id+"F0.wireOp",EDGE,"E10.30.0")])],"isStart":false});
            var Q24;
            Q24=makeQuery(id+"F2.opExtrude","CAP_FACE",FACE,{"disambiguationData":[OSD([sQuery(id+"F0.wireOp",EDGE,"E10.31.0")])],"isStart":false});
            var Q25;
            Q25=makeQuery(id+"F2.opExtrude","CAP_FACE",FACE,{"disambiguationData":[OSD([sQuery(id+"F0.wireOp",EDGE,"E10.32.0")])],"isStart":false});
            var Q26;
            Q26=makeQuery(id+"F2.opExtrude","CAP_FACE",FACE,{"disambiguationData":[OSD([sQuery(id+"F0.wireOp",EDGE,"E10.33.0")])],"isStart":false});
            var Q27;
            Q27=makeQuery(id+"F2.opExtrude","CAP_FACE",FACE,{"disambiguationData":[OSD([sQuery(id+"F0.wireOp",EDGE,"E10.34.0")])],"isStart":false});
            var Q28;
            Q28=makeQuery(id+"F2.opExtrude","CAP_FACE",FACE,{"disambiguationData":[OSD([sQuery(id+"F0.wireOp",EDGE,"E9")])],"isStart":false});
            var Q29;
            Q29=makeQuery(id+"F2.opExtrude","CAP_FACE",FACE,{"disambiguationData":[OSD([sQuery(id+"F0.wireOp",EDGE,"E10.1.0")])],"isStart":false});
            var Q30;
            Q30=makeQuery(id+"F2.opExtrude","CAP_FACE",FACE,{"disambiguationData":[OSD([sQuery(id+"F0.wireOp",EDGE,"E10.2.0")])],"isStart":false});
            var Q31;
            Q31=makeQuery(id+"F2.opExtrude","CAP_FACE",FACE,{"disambiguationData":[OSD([sQuery(id+"F0.wireOp",EDGE,"E10.3.0")])],"isStart":false});
            var Q32;
            Q32=makeQuery(id+"F2.opExtrude","CAP_FACE",FACE,{"disambiguationData":[OSD([sQuery(id+"F0.wireOp",EDGE,"E10.4.0")])],"isStart":false});
            var Q33;
            Q33=makeQuery(id+"F2.opExtrude","CAP_FACE",FACE,{"disambiguationData":[OSD([sQuery(id+"F0.wireOp",EDGE,"E10.5.0")])],"isStart":false});
            var Q34;
            Q34=makeQuery(id+"F2.opExtrude","CAP_FACE",FACE,{"disambiguationData":[OSD([sQuery(id+"F0.wireOp",EDGE,"E10.6.0")])],"isStart":false});
            fillet(context, id + "F4", {"entities" : qUnion([Q0, Q1, Q2, Q3, Q4, Q5, Q6, Q7, Q8, Q9, Q10, Q11, Q12, Q13, Q14, Q15, Q16, Q17, Q18, Q19, Q20, Q21, Q22, Q23, Q24, Q25, Q26, Q27, Q28, Q29, Q30, Q31, Q32, Q33, Q34]), "radius" : 1.14 * mm, "tangentPropagation" : true, "allowEdgeOverflow" : false});
        }
        {
            var Q0;
            Q0=makeQuery(id+"F3.opExtrude","CAP_FACE",FACE,{"disambiguationData":[OSD([sQuery(id+"F0.wireOp",EDGE,"E4.0"),sQuery(id+"F0.wireOp",EDGE,"E8.23.0"),sQuery(id+"F0.wireOp",EDGE,"E8.23.1"),sQuery(id+"F0.wireOp",EDGE,"E8.23.2")])],"isStart":false});
            var Q1;
            Q1=makeQuery(id+"F3.opExtrude","CAP_FACE",FACE,{"disambiguationData":[OSD([sQuery(id+"F0.wireOp",EDGE,"E4.0"),sQuery(id+"F0.wireOp",EDGE,"E8.24.0"),sQuery(id+"F0.wireOp",EDGE,"E8.24.1"),sQuery(id+"F0.wireOp",EDGE,"E8.24.2")])],"isStart":false});
            var Q2;
            Q2=makeQuery(id+"F3.opExtrude","CAP_FACE",FACE,{"disambiguationData":[OSD([sQuery(id+"F0.wireOp",EDGE,"E4.0"),sQuery(id+"F0.wireOp",EDGE,"E8.25.0"),sQuery(id+"F0.wireOp",EDGE,"E8.25.1"),sQuery(id+"F0.wireOp",EDGE,"E8.25.2")])],"isStart":false});
            var Q3;
            Q3=makeQuery(id+"F3.opExtrude","CAP_FACE",FACE,{"disambiguationData":[OSD([sQuery(id+"F0.wireOp",EDGE,"E4.0"),sQuery(id+"F0.wireOp",EDGE,"E8.26.0"),sQuery(id+"F0.wireOp",EDGE,"E8.26.1"),sQuery(id+"F0.wireOp",EDGE,"E8.26.2")])],"isStart":false});
            var Q4;
            Q4=makeQuery(id+"F3.opExtrude","CAP_FACE",FACE,{"disambiguationData":[OSD([sQuery(id+"F0.wireOp",EDGE,"E4.0"),sQuery(id+"F0.wireOp",EDGE,"E8.27.0"),sQuery(id+"F0.wireOp",EDGE,"E8.27.1"),sQuery(id+"F0.wireOp",EDGE,"E8.27.2")])],"isStart":false});
            var Q5;
            Q5=makeQuery(id+"F3.opExtrude","CAP_FACE",FACE,{"disambiguationData":[OSD([sQuery(id+"F0.wireOp",EDGE,"E4.0"),sQuery(id+"F0.wireOp",EDGE,"E8.28.0"),sQuery(id+"F0.wireOp",EDGE,"E8.28.1"),sQuery(id+"F0.wireOp",EDGE,"E8.28.2")])],"isStart":false});
            var Q6;
            Q6=makeQuery(id+"F3.opExtrude","CAP_FACE",FACE,{"disambiguationData":[OSD([sQuery(id+"F0.wireOp",EDGE,"E4.0"),sQuery(id+"F0.wireOp",EDGE,"E8.29.0"),sQuery(id+"F0.wireOp",EDGE,"E8.29.1"),sQuery(id+"F0.wireOp",EDGE,"E8.29.2")])],"isStart":false});
            var Q7;
            Q7=makeQuery(id+"F3.opExtrude","CAP_FACE",FACE,{"disambiguationData":[OSD([sQuery(id+"F0.wireOp",EDGE,"E4.0"),sQuery(id+"F0.wireOp",EDGE,"E8.30.0"),sQuery(id+"F0.wireOp",EDGE,"E8.30.1"),sQuery(id+"F0.wireOp",EDGE,"E8.30.2")])],"isStart":false});
            var Q8;
            Q8=makeQuery(id+"F3.opExtrude","CAP_FACE",FACE,{"disambiguationData":[OSD([sQuery(id+"F0.wireOp",EDGE,"E4.0"),sQuery(id+"F0.wireOp",EDGE,"E8.31.0"),sQuery(id+"F0.wireOp",EDGE,"E8.31.1"),sQuery(id+"F0.wireOp",EDGE,"E8.31.2")])],"isStart":false});
            var Q9;
            Q9=makeQuery(id+"F3.opExtrude","CAP_FACE",FACE,{"disambiguationData":[OSD([sQuery(id+"F0.wireOp",EDGE,"E4.0"),sQuery(id+"F0.wireOp",EDGE,"E8.32.0"),sQuery(id+"F0.wireOp",EDGE,"E8.32.1"),sQuery(id+"F0.wireOp",EDGE,"E8.32.2")])],"isStart":false});
            var Q10;
            Q10=makeQuery(id+"F3.opExtrude","CAP_FACE",FACE,{"disambiguationData":[OSD([sQuery(id+"F0.wireOp",EDGE,"E4.0"),sQuery(id+"F0.wireOp",EDGE,"E8.33.0"),sQuery(id+"F0.wireOp",EDGE,"E8.33.1"),sQuery(id+"F0.wireOp",EDGE,"E8.33.2")])],"isStart":false});
            var Q11;
            Q11=makeQuery(id+"F3.opExtrude","CAP_FACE",FACE,{"disambiguationData":[OSD([sQuery(id+"F0.wireOp",EDGE,"E4.0"),sQuery(id+"F0.wireOp",EDGE,"E8.34.0"),sQuery(id+"F0.wireOp",EDGE,"E8.34.1"),sQuery(id+"F0.wireOp",EDGE,"E8.34.2")])],"isStart":false});
            var Q12;
            Q12=makeQuery(id+"F3.opExtrude","CAP_FACE",FACE,{"disambiguationData":[OSD([sQuery(id+"F0.wireOp",EDGE,"E4.0"),sQuery(id+"F0.wireOp",EDGE,"E5"),sQuery(id+"F0.wireOp",EDGE,"E6"),sQuery(id+"F0.wireOp",EDGE,"E7")])],"isStart":false});
            var Q13;
            Q13=makeQuery(id+"F3.opExtrude","CAP_FACE",FACE,{"disambiguationData":[OSD([sQuery(id+"F0.wireOp",EDGE,"E4.0"),sQuery(id+"F0.wireOp",EDGE,"E8.1.0"),sQuery(id+"F0.wireOp",EDGE,"E8.1.1"),sQuery(id+"F0.wireOp",EDGE,"E8.1.2")])],"isStart":false});
            var Q14;
            Q14=makeQuery(id+"F3.opExtrude","CAP_FACE",FACE,{"disambiguationData":[OSD([sQuery(id+"F0.wireOp",EDGE,"E4.0"),sQuery(id+"F0.wireOp",EDGE,"E8.2.0"),sQuery(id+"F0.wireOp",EDGE,"E8.2.1"),sQuery(id+"F0.wireOp",EDGE,"E8.2.2")])],"isStart":false});
            var Q15;
            Q15=makeQuery(id+"F3.opExtrude","CAP_FACE",FACE,{"disambiguationData":[OSD([sQuery(id+"F0.wireOp",EDGE,"E4.0"),sQuery(id+"F0.wireOp",EDGE,"E8.3.0"),sQuery(id+"F0.wireOp",EDGE,"E8.3.1"),sQuery(id+"F0.wireOp",EDGE,"E8.3.2")])],"isStart":false});
            var Q16;
            Q16=makeQuery(id+"F3.opExtrude","CAP_FACE",FACE,{"disambiguationData":[OSD([sQuery(id+"F0.wireOp",EDGE,"E4.0"),sQuery(id+"F0.wireOp",EDGE,"E8.4.0"),sQuery(id+"F0.wireOp",EDGE,"E8.4.1"),sQuery(id+"F0.wireOp",EDGE,"E8.4.2")])],"isStart":false});
            var Q17;
            Q17=makeQuery(id+"F3.opExtrude","CAP_FACE",FACE,{"disambiguationData":[OSD([sQuery(id+"F0.wireOp",EDGE,"E4.0"),sQuery(id+"F0.wireOp",EDGE,"E8.5.0"),sQuery(id+"F0.wireOp",EDGE,"E8.5.1"),sQuery(id+"F0.wireOp",EDGE,"E8.5.2")])],"isStart":false});
            var Q18;
            Q18=makeQuery(id+"F3.opExtrude","CAP_FACE",FACE,{"disambiguationData":[OSD([sQuery(id+"F0.wireOp",EDGE,"E4.0"),sQuery(id+"F0.wireOp",EDGE,"E8.6.0"),sQuery(id+"F0.wireOp",EDGE,"E8.6.1"),sQuery(id+"F0.wireOp",EDGE,"E8.6.2")])],"isStart":false});
            var Q19;
            Q19=makeQuery(id+"F3.opExtrude","CAP_FACE",FACE,{"disambiguationData":[OSD([sQuery(id+"F0.wireOp",EDGE,"E4.0"),sQuery(id+"F0.wireOp",EDGE,"E8.7.0"),sQuery(id+"F0.wireOp",EDGE,"E8.7.1"),sQuery(id+"F0.wireOp",EDGE,"E8.7.2")])],"isStart":false});
            var Q20;
            Q20=makeQuery(id+"F3.opExtrude","CAP_FACE",FACE,{"disambiguationData":[OSD([sQuery(id+"F0.wireOp",EDGE,"E4.0"),sQuery(id+"F0.wireOp",EDGE,"E8.8.0"),sQuery(id+"F0.wireOp",EDGE,"E8.8.1"),sQuery(id+"F0.wireOp",EDGE,"E8.8.2")])],"isStart":false});
            var Q21;
            Q21=makeQuery(id+"F3.opExtrude","CAP_FACE",FACE,{"disambiguationData":[OSD([sQuery(id+"F0.wireOp",EDGE,"E4.0"),sQuery(id+"F0.wireOp",EDGE,"E8.9.0"),sQuery(id+"F0.wireOp",EDGE,"E8.9.1"),sQuery(id+"F0.wireOp",EDGE,"E8.9.2")])],"isStart":false});
            var Q22;
            Q22=makeQuery(id+"F3.opExtrude","CAP_FACE",FACE,{"disambiguationData":[OSD([sQuery(id+"F0.wireOp",EDGE,"E4.0"),sQuery(id+"F0.wireOp",EDGE,"E8.10.0"),sQuery(id+"F0.wireOp",EDGE,"E8.10.1"),sQuery(id+"F0.wireOp",EDGE,"E8.10.2")])],"isStart":false});
            var Q23;
            Q23=makeQuery(id+"F3.opExtrude","CAP_FACE",FACE,{"disambiguationData":[OSD([sQuery(id+"F0.wireOp",EDGE,"E4.0"),sQuery(id+"F0.wireOp",EDGE,"E8.11.0"),sQuery(id+"F0.wireOp",EDGE,"E8.11.1"),sQuery(id+"F0.wireOp",EDGE,"E8.11.2")])],"isStart":false});
            var Q24;
            Q24=makeQuery(id+"F3.opExtrude","CAP_FACE",FACE,{"disambiguationData":[OSD([sQuery(id+"F0.wireOp",EDGE,"E4.0"),sQuery(id+"F0.wireOp",EDGE,"E8.12.0"),sQuery(id+"F0.wireOp",EDGE,"E8.12.1"),sQuery(id+"F0.wireOp",EDGE,"E8.12.2")])],"isStart":false});
            var Q25;
            Q25=makeQuery(id+"F3.opExtrude","CAP_FACE",FACE,{"disambiguationData":[OSD([sQuery(id+"F0.wireOp",EDGE,"E4.0"),sQuery(id+"F0.wireOp",EDGE,"E8.13.0"),sQuery(id+"F0.wireOp",EDGE,"E8.13.1"),sQuery(id+"F0.wireOp",EDGE,"E8.13.2")])],"isStart":false});
            var Q26;
            Q26=makeQuery(id+"F3.opExtrude","CAP_FACE",FACE,{"disambiguationData":[OSD([sQuery(id+"F0.wireOp",EDGE,"E4.0"),sQuery(id+"F0.wireOp",EDGE,"E8.14.0"),sQuery(id+"F0.wireOp",EDGE,"E8.14.1"),sQuery(id+"F0.wireOp",EDGE,"E8.14.2")])],"isStart":false});
            var Q27;
            Q27=makeQuery(id+"F3.opExtrude","CAP_FACE",FACE,{"disambiguationData":[OSD([sQuery(id+"F0.wireOp",EDGE,"E4.0"),sQuery(id+"F0.wireOp",EDGE,"E8.15.0"),sQuery(id+"F0.wireOp",EDGE,"E8.15.1"),sQuery(id+"F0.wireOp",EDGE,"E8.15.2")])],"isStart":false});
            var Q28;
            Q28=makeQuery(id+"F3.opExtrude","CAP_FACE",FACE,{"disambiguationData":[OSD([sQuery(id+"F0.wireOp",EDGE,"E4.0"),sQuery(id+"F0.wireOp",EDGE,"E8.16.0"),sQuery(id+"F0.wireOp",EDGE,"E8.16.1"),sQuery(id+"F0.wireOp",EDGE,"E8.16.2")])],"isStart":false});
            var Q29;
            Q29=makeQuery(id+"F3.opExtrude","CAP_FACE",FACE,{"disambiguationData":[OSD([sQuery(id+"F0.wireOp",EDGE,"E4.0"),sQuery(id+"F0.wireOp",EDGE,"E8.17.0"),sQuery(id+"F0.wireOp",EDGE,"E8.17.1"),sQuery(id+"F0.wireOp",EDGE,"E8.17.2")])],"isStart":false});
            var Q30;
            Q30=makeQuery(id+"F3.opExtrude","CAP_FACE",FACE,{"disambiguationData":[OSD([sQuery(id+"F0.wireOp",EDGE,"E4.0"),sQuery(id+"F0.wireOp",EDGE,"E8.18.0"),sQuery(id+"F0.wireOp",EDGE,"E8.18.1"),sQuery(id+"F0.wireOp",EDGE,"E8.18.2")])],"isStart":false});
            var Q31;
            Q31=makeQuery(id+"F3.opExtrude","CAP_FACE",FACE,{"disambiguationData":[OSD([sQuery(id+"F0.wireOp",EDGE,"E4.0"),sQuery(id+"F0.wireOp",EDGE,"E8.19.0"),sQuery(id+"F0.wireOp",EDGE,"E8.19.1"),sQuery(id+"F0.wireOp",EDGE,"E8.19.2")])],"isStart":false});
            var Q32;
            Q32=makeQuery(id+"F3.opExtrude","CAP_FACE",FACE,{"disambiguationData":[OSD([sQuery(id+"F0.wireOp",EDGE,"E4.0"),sQuery(id+"F0.wireOp",EDGE,"E8.20.0"),sQuery(id+"F0.wireOp",EDGE,"E8.20.1"),sQuery(id+"F0.wireOp",EDGE,"E8.20.2")])],"isStart":false});
            var Q33;
            Q33=makeQuery(id+"F3.opExtrude","CAP_FACE",FACE,{"disambiguationData":[OSD([sQuery(id+"F0.wireOp",EDGE,"E4.0"),sQuery(id+"F0.wireOp",EDGE,"E8.21.0"),sQuery(id+"F0.wireOp",EDGE,"E8.21.1"),sQuery(id+"F0.wireOp",EDGE,"E8.21.2")])],"isStart":false});
            var Q34;
            Q34=makeQuery(id+"F3.opExtrude","CAP_FACE",FACE,{"disambiguationData":[OSD([sQuery(id+"F0.wireOp",EDGE,"E4.0"),sQuery(id+"F0.wireOp",EDGE,"E8.22.0"),sQuery(id+"F0.wireOp",EDGE,"E8.22.1"),sQuery(id+"F0.wireOp",EDGE,"E8.22.2")])],"isStart":false});
            fillet(context, id + "F5", {"entities" : qUnion([Q0, Q1, Q2, Q3, Q4, Q5, Q6, Q7, Q8, Q9, Q10, Q11, Q12, Q13, Q14, Q15, Q16, Q17, Q18, Q19, Q20, Q21, Q22, Q23, Q24, Q25, Q26, Q27, Q28, Q29, Q30, Q31, Q32, Q33, Q34]), "radius" : 0.48 * mm, "tangentPropagation" : true, "allowEdgeOverflow" : false});
        }
        {
            var Q0;
            Q0=makeQuery(id+"F1.opExtrude","CAP_EDGE",EDGE,{"disambiguationData":[OSD([sQuery(id+"F0.wireOp",EDGE,"E4.0")])],"isStart":false});
            var Q1;
            Q1=makeQuery(id+"F1.opExtrude","CAP_EDGE",EDGE,{"disambiguationData":[OSD([sQuery(id+"F0.wireOp",EDGE,"E3")])],"isStart":false});
            fillet(context, id + "F6", {"entities" : qUnion([Q0, Q1]), "radius" : 0.76 * mm, "tangentPropagation" : true, "allowEdgeOverflow" : false});
        }
        {
            var Q0;
            Q0=makeQuery(id+"F1.opExtrude","CAP_EDGE",EDGE,{"disambiguationData":[OSD([sQuery(id+"F0.wireOp",EDGE,"E18")])],"isStart":false});
            var Q1;
            {var subQ0=sQuery(id+"F0.wireOp",EDGE,"E20");Q1=makeQuery(id+"F1.opExtrude","CAP_EDGE",EDGE,{"disambiguationData":[OSD([subQ0]),TDD([makeQuery(id+"F0.imprint","IMPRINT",EDGE,{"disambiguationData":[TD([[makeQuery(id+"F0.imprint","INTERSECT",VERTEX,{"derivedFrom":[sQuery(id+"F0.wireOp",EDGE,"E18"),subQ0]}),-1.0]])],"derivedFrom":subQ0})])],"isStart":false});}
            var Q2;
            {var subQ0=sQuery(id+"F0.wireOp",EDGE,"E12.0");Q2=makeQuery(id+"F1.opExtrude","CAP_EDGE",EDGE,{"disambiguationData":[OSD([subQ0]),TDD([makeQuery(id+"F0.imprint","IMPRINT",EDGE,{"disambiguationData":[TD([[makeQuery(id+"F0.imprint","INTERSECT",VERTEX,{"derivedFrom":[subQ0,sQuery(id+"F0.wireOp",EDGE,"E13")]}),-1.0]])],"derivedFrom":subQ0})])],"isStart":false});}
            var Q3;
            {var subQ0=sQuery(id+"F0.wireOp",EDGE,"E11.0");Q3=makeQuery(id+"F1.opExtrude","CAP_EDGE",EDGE,{"disambiguationData":[OSD([subQ0]),TDD([makeQuery(id+"F0.imprint","IMPRINT",EDGE,{"disambiguationData":[TD([[makeQuery(id+"F0.imprint","INTERSECT",VERTEX,{"derivedFrom":[subQ0,sQuery(id+"F0.wireOp",EDGE,"E13")]}),-1.0]])],"derivedFrom":subQ0})])],"isStart":false});}
            var Q4;
            {var subQ0=sQuery(id+"F0.wireOp",EDGE,"E20");Q4=makeQuery(id+"F1.opExtrude","CAP_EDGE",EDGE,{"disambiguationData":[OSD([subQ0]),TDD([makeQuery(id+"F0.imprint","IMPRINT",EDGE,{"disambiguationData":[TD([[makeQuery(id+"F0.imprint","INTERSECT",VERTEX,{"derivedFrom":[sQuery(id+"F0.wireOp",EDGE,"E19"),subQ0]}),1.0]])],"derivedFrom":subQ0})])],"isStart":false});}
            var Q5;
            Q5=makeQuery(id+"F1.opExtrude","CAP_EDGE",EDGE,{"disambiguationData":[OSD([sQuery(id+"F0.wireOp",EDGE,"E19")])],"isStart":false});
            fillet(context, id + "F7", {"entities" : qUnion([Q0, Q1, Q2, Q3, Q4, Q5]), "radius" : 1.27 * mm, "tangentPropagation" : true, "allowEdgeOverflow" : false});
        }
        {
            var Q0;
            Q0=qCreatedBy(makeId("Right.planeOp"),FACE);
            var sketch = newSketch(context, id + "F8", { "sketchPlane" : qUnion([Q0])});
            skLineSegment(sketch, "E21", {"start": v(0, 0) * mm, "end": v(0, 32.7) * mm});
            skSolve(sketch);
        }
        {
            var Q0;
            Q0=makeQuery(id+"F1.opExtrude","SWEPT_BODY",BODY,{"disambiguationData":[OSD([sQuery(id+"F0.wireOp",EDGE,"E3"),sQuery(id+"F0.wireOp",EDGE,"E4.0"),sQuery(id+"F0.wireOp",EDGE,"E9"),sQuery(id+"F0.wireOp",EDGE,"E10.1.0"),sQuery(id+"F0.wireOp",EDGE,"E10.2.0"),sQuery(id+"F0.wireOp",EDGE,"E10.3.0"),sQuery(id+"F0.wireOp",EDGE,"E10.4.0"),sQuery(id+"F0.wireOp",EDGE,"E10.5.0"),sQuery(id+"F0.wireOp",EDGE,"E10.6.0"),sQuery(id+"F0.wireOp",EDGE,"E10.7.0"),sQuery(id+"F0.wireOp",EDGE,"E10.8.0"),sQuery(id+"F0.wireOp",EDGE,"E10.9.0"),sQuery(id+"F0.wireOp",EDGE,"E10.10.0"),sQuery(id+"F0.wireOp",EDGE,"E10.11.0"),sQuery(id+"F0.wireOp",EDGE,"E10.12.0"),sQuery(id+"F0.wireOp",EDGE,"E10.13.0"),sQuery(id+"F0.wireOp",EDGE,"E10.14.0"),sQuery(id+"F0.wireOp",EDGE,"E10.15.0"),sQuery(id+"F0.wireOp",EDGE,"E10.16.0"),sQuery(id+"F0.wireOp",EDGE,"E10.17.0"),sQuery(id+"F0.wireOp",EDGE,"E10.18.0"),sQuery(id+"F0.wireOp",EDGE,"E10.19.0"),sQuery(id+"F0.wireOp",EDGE,"E10.20.0"),sQuery(id+"F0.wireOp",EDGE,"E10.21.0"),sQuery(id+"F0.wireOp",EDGE,"E10.22.0"),sQuery(id+"F0.wireOp",EDGE,"E10.23.0"),sQuery(id+"F0.wireOp",EDGE,"E10.24.0"),sQuery(id+"F0.wireOp",EDGE,"E10.25.0"),sQuery(id+"F0.wireOp",EDGE,"E10.26.0"),sQuery(id+"F0.wireOp",EDGE,"E10.27.0"),sQuery(id+"F0.wireOp",EDGE,"E10.28.0"),sQuery(id+"F0.wireOp",EDGE,"E10.29.0"),sQuery(id+"F0.wireOp",EDGE,"E10.30.0"),sQuery(id+"F0.wireOp",EDGE,"E10.31.0"),sQuery(id+"F0.wireOp",EDGE,"E10.32.0"),sQuery(id+"F0.wireOp",EDGE,"E10.33.0"),sQuery(id+"F0.wireOp",EDGE,"E10.34.0"),sQuery(id+"F0.wireOp",EDGE,"E11.0"),sQuery(id+"F0.wireOp",EDGE,"E12.0"),sQuery(id+"F0.wireOp",EDGE,"E13"),sQuery(id+"F0.wireOp",EDGE,"E18"),sQuery(id+"F0.wireOp",EDGE,"E19"),sQuery(id+"F0.wireOp",EDGE,"E20")])]});
            var Q1;
            Q1=sQuery(id+"F8.wireOp",EDGE,"E21");
            circularPattern(context, id + "F9", {"entities" : qUnion([Q0]), "axis" : qUnion([Q1]), "angle" : 360 * degree, "instanceCount" : 12, "equalSpace" : true, "computeTransformsWithoutBuiltin" : true});
        }
        {
            var Q0;
            Q0=qCreatedBy(makeId("Top.planeOp"),FACE);
            var sketch = newSketch(context, id + "F10", { "sketchPlane" : qUnion([Q0])});
            skCircle(sketch, "E22", {"center": v(0, 0) * mm, "radius": 28.58 * mm});
            skCircle(sketch, "E23", {"center": v(0, 0) * mm, "radius": 13.02 * mm});
            skSolve(sketch);
        }
        {
            var Q0;
            Q0=makeQuery(id+"F10.imprint","IMPRINT",FACE,{"disambiguationData":[TD([[makeQuery(id+"F10.imprint","IMPRINT",EDGE,{"derivedFrom":sQuery(id+"F10.wireOp",EDGE,"E22")}),1.0]])]});
            var Q1;
            Q1=makeQuery(id+"F9.opPattern","COPY",FACE,{"derivedFrom":makeQuery(id+"F6.opFillet","SPLIT",FACE,{"disambiguationData":[OD(33.0)],"derivedFrom":makeQuery(id+"F1.opExtrude","CAP_FACE",FACE,{"disambiguationData":[OSD([sQuery(id+"F0.wireOp",EDGE,"E3"),sQuery(id+"F0.wireOp",EDGE,"E4.0"),sQuery(id+"F0.wireOp",EDGE,"E9"),sQuery(id+"F0.wireOp",EDGE,"E10.1.0"),sQuery(id+"F0.wireOp",EDGE,"E10.2.0"),sQuery(id+"F0.wireOp",EDGE,"E10.3.0"),sQuery(id+"F0.wireOp",EDGE,"E10.4.0"),sQuery(id+"F0.wireOp",EDGE,"E10.5.0"),sQuery(id+"F0.wireOp",EDGE,"E10.6.0"),sQuery(id+"F0.wireOp",EDGE,"E10.7.0"),sQuery(id+"F0.wireOp",EDGE,"E10.8.0"),sQuery(id+"F0.wireOp",EDGE,"E10.9.0"),sQuery(id+"F0.wireOp",EDGE,"E10.10.0"),sQuery(id+"F0.wireOp",EDGE,"E10.11.0"),sQuery(id+"F0.wireOp",EDGE,"E10.12.0"),sQuery(id+"F0.wireOp",EDGE,"E10.13.0"),sQuery(id+"F0.wireOp",EDGE,"E10.14.0"),sQuery(id+"F0.wireOp",EDGE,"E10.15.0"),sQuery(id+"F0.wireOp",EDGE,"E10.16.0"),sQuery(id+"F0.wireOp",EDGE,"E10.17.0"),sQuery(id+"F0.wireOp",EDGE,"E10.18.0"),sQuery(id+"F0.wireOp",EDGE,"E10.19.0"),sQuery(id+"F0.wireOp",EDGE,"E10.20.0"),sQuery(id+"F0.wireOp",EDGE,"E10.21.0"),sQuery(id+"F0.wireOp",EDGE,"E10.22.0"),sQuery(id+"F0.wireOp",EDGE,"E10.23.0"),sQuery(id+"F0.wireOp",EDGE,"E10.24.0"),sQuery(id+"F0.wireOp",EDGE,"E10.25.0"),sQuery(id+"F0.wireOp",EDGE,"E10.26.0"),sQuery(id+"F0.wireOp",EDGE,"E10.27.0"),sQuery(id+"F0.wireOp",EDGE,"E10.28.0"),sQuery(id+"F0.wireOp",EDGE,"E10.29.0"),sQuery(id+"F0.wireOp",EDGE,"E10.30.0"),sQuery(id+"F0.wireOp",EDGE,"E10.31.0"),sQuery(id+"F0.wireOp",EDGE,"E10.32.0"),sQuery(id+"F0.wireOp",EDGE,"E10.33.0"),sQuery(id+"F0.wireOp",EDGE,"E10.34.0"),sQuery(id+"F0.wireOp",EDGE,"E11.0"),sQuery(id+"F0.wireOp",EDGE,"E12.0"),sQuery(id+"F0.wireOp",EDGE,"E13"),sQuery(id+"F0.wireOp",EDGE,"E18"),sQuery(id+"F0.wireOp",EDGE,"E19"),sQuery(id+"F0.wireOp",EDGE,"E20")])],"isStart":false})}),"instanceName":"5"});
            extrude(context, id + "F11", {"entities" : qUnion([Q0]), "endBound" : BoundingType.UP_TO_SURFACE, "depth" : 25.4 * mm, "endBoundEntityFace" : qUnion([Q1]), "offsetDistance" : 25.4 * mm});
        }
        {
            var Q0;
            Q0=makeQuery(id+"F11.opExtrude","CAP_FACE",FACE,{"disambiguationData":[OSD([sQuery(id+"F10.wireOp",EDGE,"E22"),sQuery(id+"F10.wireOp",EDGE,"E23")])],"isStart":false});
            var sketch = newSketch(context, id + "F12", { "sketchPlane" : qUnion([Q0])});
            skLineSegment(sketch, "E24", {"start": v(-6.92, 11.03) * mm, "end": v(6.92, 11.03) * mm});
            skSolve(sketch);
        }
        {
            var Q0;
            {var subQ0=sQuery(id+"F12.wireOp",EDGE,"E24");Q0=makeQuery(id+"F12.imprint","IMPRINT",FACE,{"disambiguationData":[TD([[makeQuery(id+"F12.imprint","IMPRINT",EDGE,{"derivedFrom":subQ0}),1.0]])]});}
            var Q1;
            Q1=makeQuery(id+"F11.opExtrude","CAP_FACE",FACE,{"disambiguationData":[OSD([sQuery(id+"F10.wireOp",EDGE,"E22"),sQuery(id+"F10.wireOp",EDGE,"E23")])],"isStart":true});
            extrude(context, id + "F13", {"entities" : qUnion([Q0]), "operationType" : NewBodyOperationType.ADD, "endBound" : BoundingType.UP_TO_SURFACE, "oppositeDirection" : true, "depth" : 25.4 * mm, "endBoundEntityFace" : qUnion([Q1]), "offsetDistance" : 25.4 * mm});
        }
    });
